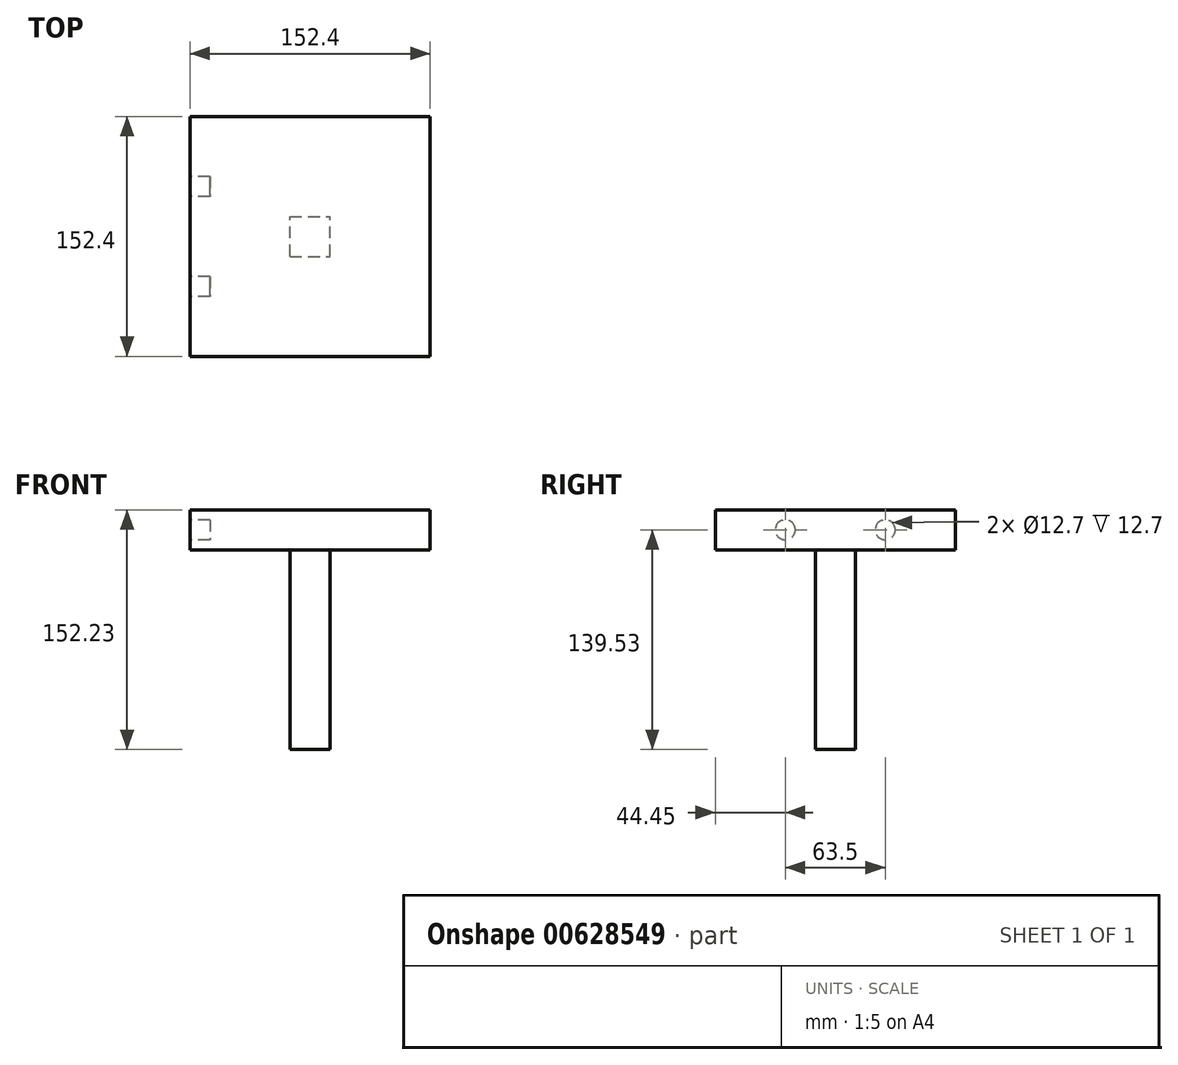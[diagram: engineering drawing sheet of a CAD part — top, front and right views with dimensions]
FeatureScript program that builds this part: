
annotation { "Feature Type Name" : "Feature", "Feature Type Description" : "" }
export const myFeature = defineFeature(function(context is Context, id is Id, definition is map)
    precondition{}
    {
        {
            var Q0;
            Q0=qCreatedBy(makeId("Front.planeOp"),FACE);
            var sketch = newSketch(context, id + "F0", { "sketchPlane" : qUnion([Q0])});
            skLineSegment(sketch, "E0.bottom", {"start": v(-12.7, 76.2) * mm, "end": v(12.7, 76.2) * mm});
            skLineSegment(sketch, "E0.top", {"start": v(-12.7, -76.2) * mm, "end": v(12.7, -76.2) * mm});
            skLineSegment(sketch, "E0.left", {"start": v(-12.7, 76.2) * mm, "end": v(-12.7, 76.03) * mm});
            skLineSegment(sketch, "E0.right", {"start": v(12.7, 76.2) * mm, "end": v(12.7, 76.03) * mm});
            skPoint(sketch, "E0.middle", {"position": v(0, 0) * mm});
            skLineSegment(sketch, "E1.bottom", {"start": v(-76.2, 76.03) * mm, "end": v(76.2, 76.03) * mm});
            skLineSegment(sketch, "E1.top", {"start": v(-76.2, 50.63) * mm, "end": v(76.2, 50.63) * mm});
            skLineSegment(sketch, "E1.left", {"start": v(-76.2, 76.03) * mm, "end": v(-76.2, 50.63) * mm});
            skLineSegment(sketch, "E1.right", {"start": v(76.2, 76.03) * mm, "end": v(76.2, 50.63) * mm});
            skLineSegment(sketch, "E2.trimOffspring", {"start": v(-12.7, 50.63) * mm, "end": v(-12.7, -76.2) * mm});
            skLineSegment(sketch, "E3.trimOffspring", {"start": v(12.7, 50.63) * mm, "end": v(12.7, -76.2) * mm});
            skSolve(sketch);
        }
        {
            var Q0;
            {var subQ0=sQuery(id+"F0.wireOp",EDGE,"E1.left");Q0=makeQuery(id+"F0.imprint","IMPRINT",FACE,{"disambiguationData":[TD([[makeQuery(id+"F0.imprint","IMPRINT",EDGE,{"derivedFrom":subQ0}),1.0]])]});}
            extrude(context, id + "F1", {"entities" : qUnion([Q0]), "endBound" : BoundingType.SYMMETRIC, "depth" : 152.4 * mm, "offsetDistance" : 25.4 * mm});
        }
        {
            var Q0;
            Q0=makeQuery(id+"F0.imprint","IMPRINT",FACE,{"disambiguationData":[TD([[makeQuery(id+"F0.imprint","IMPRINT",EDGE,{"derivedFrom":sQuery(id+"F0.wireOp",EDGE,"E0.top")}),1.0]])]});
            extrude(context, id + "F2", {"entities" : qUnion([Q0]), "operationType" : NewBodyOperationType.ADD, "endBound" : BoundingType.SYMMETRIC, "depth" : 25.4 * mm, "offsetDistance" : 25.4 * mm});
        }
        {
            var Q0;
            Q0=makeQuery(id+"F1.opExtrude","SWEPT_FACE",FACE,{"disambiguationData":[OSD([sQuery(id+"F0.wireOp",EDGE,"E1.left")])]});
            var sketch = newSketch(context, id + "F3", { "sketchPlane" : qUnion([Q0])});
            skCircle(sketch, "E4", {"center": v(-31.75, 63.33) * mm, "radius": 6.35 * mm});
            skPoint(sketch, "E4.centerSnap0", {"position": v(-76.2, 63.33) * mm});
            skCircle(sketch, "E5", {"center": v(31.75, 63.33) * mm, "radius": 6.35 * mm});
            skSolve(sketch);
        }
        {
            var Q0;
            Q0=makeQuery(id+"F3.imprint","IMPRINT",FACE,{"disambiguationData":[TD([[makeQuery(id+"F3.imprint","IMPRINT",EDGE,{"derivedFrom":sQuery(id+"F3.wireOp",EDGE,"E5")}),1.0]])]});
            var Q1;
            Q1=makeQuery(id+"F3.imprint","IMPRINT",FACE,{"disambiguationData":[TD([[makeQuery(id+"F3.imprint","IMPRINT",EDGE,{"derivedFrom":sQuery(id+"F3.wireOp",EDGE,"E4")}),1.0]])]});
            extrude(context, id + "F4", {"entities" : qUnion([Q0, Q1]), "operationType" : NewBodyOperationType.REMOVE, "oppositeDirection" : true, "depth" : 12.7 * mm, "offsetDistance" : 25.4 * mm});
        }
    });
